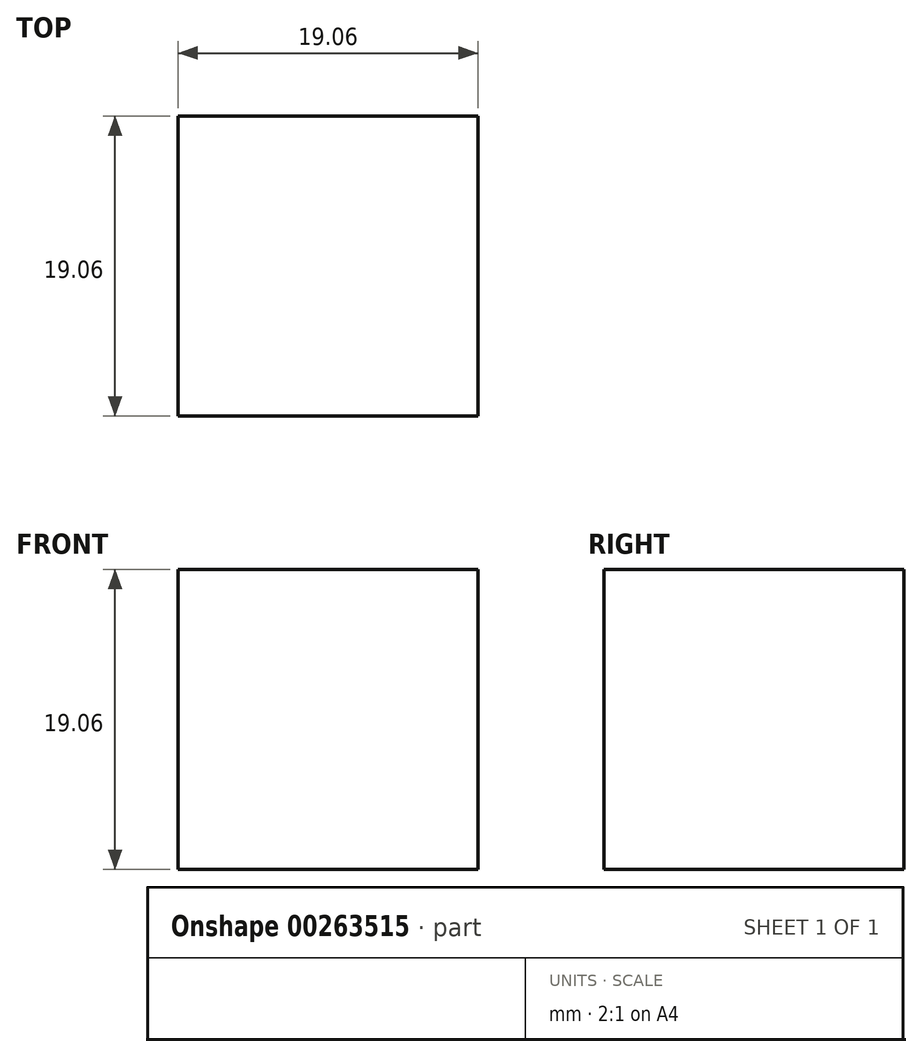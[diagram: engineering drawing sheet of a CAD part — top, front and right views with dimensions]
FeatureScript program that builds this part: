
annotation { "Feature Type Name" : "Feature", "Feature Type Description" : "" }
export const myFeature = defineFeature(function(context is Context, id is Id, definition is map)
    precondition{}
    {
        {
            var Q0;
            Q0=qCreatedBy(makeId("Front.planeOp"),FACE);
            var sketch = newSketch(context, id + "F0", { "sketchPlane" : qUnion([Q0])});
            skLineSegment(sketch, "E0.bottom", {"start": v(9.53, 9.52) * mm, "end": v(-9.53, 9.52) * mm});
            skLineSegment(sketch, "E0.top", {"start": v(9.53, -9.53) * mm, "end": v(-9.53, -9.53) * mm});
            skLineSegment(sketch, "E0.left", {"start": v(9.53, 9.52) * mm, "end": v(9.53, -9.53) * mm});
            skLineSegment(sketch, "E0.right", {"start": v(-9.53, 9.52) * mm, "end": v(-9.53, -9.53) * mm});
            skPoint(sketch, "E0.middle", {"position": v(0, 0) * mm});
            skSolve(sketch);
        }
        {
            var Q0;
            Q0=makeQuery(id+"F0.imprint","IMPRINT",FACE,{"disambiguationData":[TD([[makeQuery(id+"F0.imprint","IMPRINT",EDGE,{"derivedFrom":sQuery(id+"F0.wireOp",EDGE,"E0.bottom")}),1.0]])]});
            extrude(context, id + "F1", {"entities" : qUnion([Q0]), "endBound" : BoundingType.SYMMETRIC, "depth" : 19.05 * mm});
        }
    });
